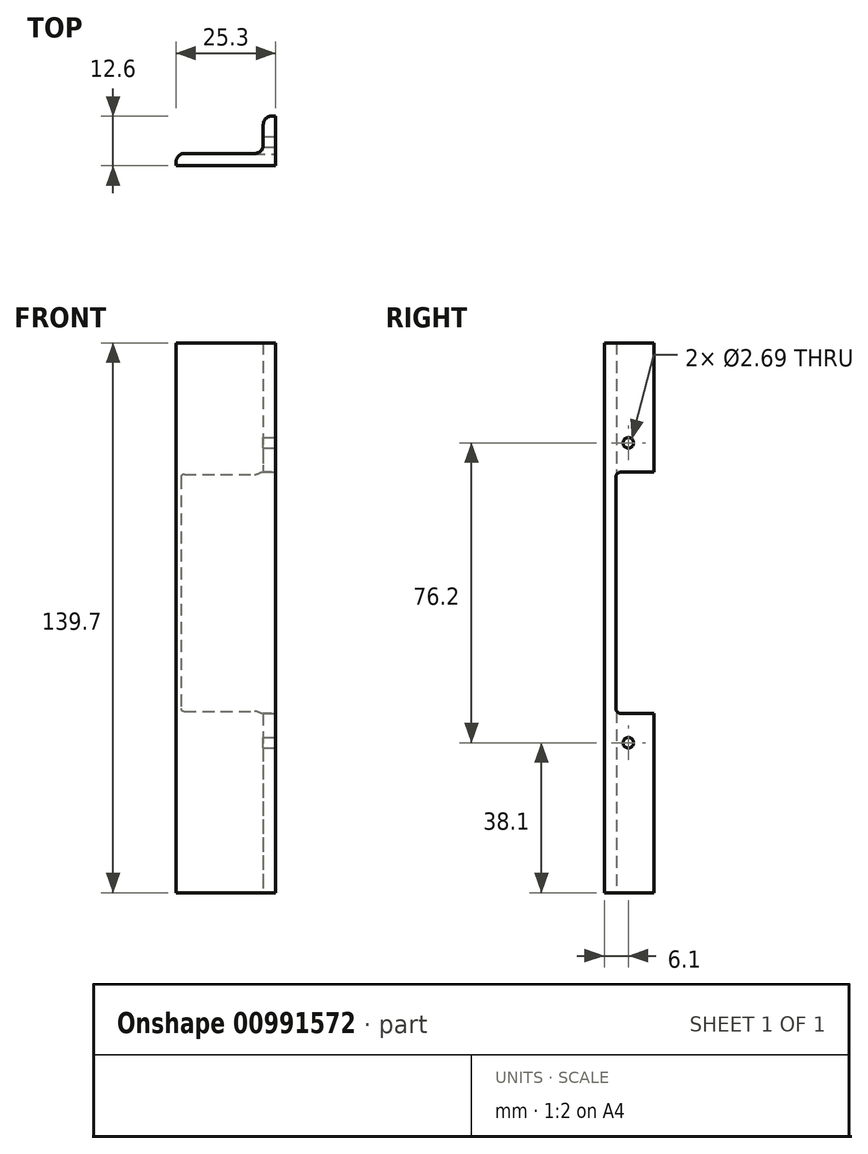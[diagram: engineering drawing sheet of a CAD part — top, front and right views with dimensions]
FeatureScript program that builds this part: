
annotation { "Feature Type Name" : "Feature", "Feature Type Description" : "" }
export const myFeature = defineFeature(function(context is Context, id is Id, definition is map)
    precondition{}
    {
        {
            var Q0;
            Q0=qCreatedBy(makeId("Top.planeOp"),FACE);
            var sketch = newSketch(context, id + "F0", { "sketchPlane" : qUnion([Q0])});
            skLineSegment(sketch, "E0", {"start": v(-15.46, -5.6) * mm, "end": v(9.84, -5.6) * mm});
            skLineSegment(sketch, "E1", {"start": v(9.84, -5.6) * mm, "end": v(9.84, 7) * mm});
            skLineSegment(sketch, "E2", {"start": v(9.84, 7) * mm, "end": v(8.87, 7) * mm});
            skLineSegment(sketch, "E3", {"start": v(6.72, 4.83) * mm, "end": v(6.72, -0.32) * mm});
            skLineSegment(sketch, "E4", {"start": v(4.56, -2.48) * mm, "end": v(-13.3, -2.48) * mm});
            skLineSegment(sketch, "E5", {"start": v(-15.46, -4.64) * mm, "end": v(-15.46, -5.6) * mm});
            skPoint(sketch, "E6.visualSharp", {"position": v(-15.46, -2.48) * mm});
            skArc(sketch, "E6.filletArc", {"start": v(-13.3, -2.48) * mm, "mid": v(-14.83, -3.11) * mm, "end": v(-15.46, -4.64) * mm});
            skPoint(sketch, "E7.visualSharp", {"position": v(6.72, 7) * mm});
            skArc(sketch, "E7.filletArc", {"start": v(8.87, 7) * mm, "mid": v(7.35, 6.36) * mm, "end": v(6.72, 4.83) * mm});
            skPoint(sketch, "E8.visualSharp", {"position": v(6.72, -2.48) * mm});
            skArc(sketch, "E8.filletArc", {"start": v(4.56, -2.48) * mm, "mid": v(6.08, -1.85) * mm, "end": v(6.72, -0.32) * mm});
            skSolve(sketch);
        }
        {
            var Q0;
            Q0 = qSketchRegion(id + "F0", true);
            extrude(context, id + "F1", {"entities" : qUnion([Q0]), "depth" : 139.7 * mm, "offsetDistance" : 25.4 * mm});
        }
        {
            var Q0;
            Q0=makeQuery(id+"F1.opExtrude","SWEPT_FACE",FACE,{"disambiguationData":[OSD([sQuery(id+"F0.wireOp",EDGE,"E1")])]});
            var sketch = newSketch(context, id + "F2", { "sketchPlane" : qUnion([Q0])});
            skCircle(sketch, "E9", {"center": v(0.49, 38.1) * mm, "radius": 1.35 * mm});
            skCircle(sketch, "E10", {"center": v(0.49, 114.3) * mm, "radius": 1.35 * mm});
            skSolve(sketch);
        }
        {
            var Q0;
            Q0 = qSketchRegion(id + "F2", true);
            extrude(context, id + "F3", {"entities" : qUnion([Q0]), "operationType" : NewBodyOperationType.REMOVE, "endBound" : BoundingType.THROUGH_ALL, "oppositeDirection" : true, "depth" : 25.4 * mm, "offsetDistance" : 25.4 * mm});
        }
        {
            var Q0;
            Q0=makeQuery(id+"F1.opExtrude","SWEPT_FACE",FACE,{"disambiguationData":[OSD([sQuery(id+"F0.wireOp",EDGE,"E1")])]});
            var sketch = newSketch(context, id + "F4", { "sketchPlane" : qUnion([Q0])});
            skLineSegment(sketch, "E11.bottom", {"start": v(7, 45.54) * mm, "end": v(-1.42, 45.54) * mm});
            skLineSegment(sketch, "E11.top", {"start": v(7, 106.86) * mm, "end": v(-1.42, 106.86) * mm});
            skLineSegment(sketch, "E11.left", {"start": v(7, 45.54) * mm, "end": v(7, 106.86) * mm});
            skLineSegment(sketch, "E11.right", {"start": v(-2.69, 46.81) * mm, "end": v(-2.69, 105.59) * mm});
            skPoint(sketch, "E12.visualSharp", {"position": v(-2.69, 45.54) * mm});
            skArc(sketch, "E12.filletArc", {"start": v(-2.69, 46.81) * mm, "mid": v(-2.31, 45.91) * mm, "end": v(-1.42, 45.54) * mm});
            skPoint(sketch, "E13.visualSharp", {"position": v(-2.69, 106.86) * mm});
            skArc(sketch, "E13.filletArc", {"start": v(-1.42, 106.86) * mm, "mid": v(-2.31, 106.49) * mm, "end": v(-2.69, 105.59) * mm});
            skSolve(sketch);
        }
        {
            var Q0;
            Q0 = qSketchRegion(id + "F4", true);
            extrude(context, id + "F5", {"entities" : qUnion([Q0]), "operationType" : NewBodyOperationType.REMOVE, "endBound" : BoundingType.THROUGH_ALL, "oppositeDirection" : true, "depth" : 25.4 * mm, "offsetDistance" : 25.4 * mm});
        }
    });
